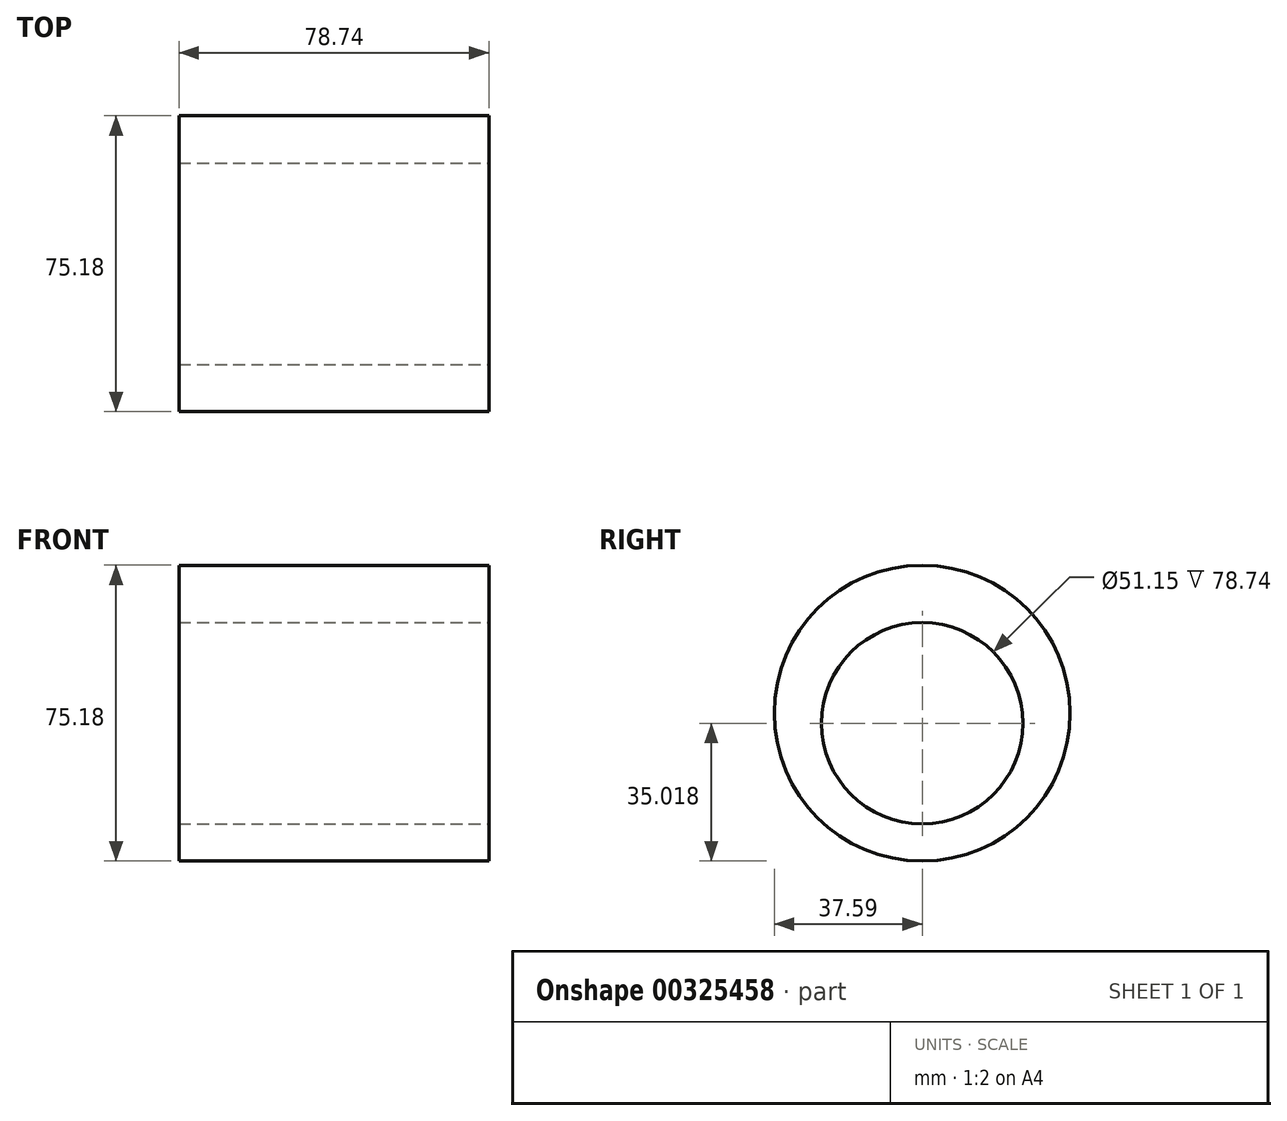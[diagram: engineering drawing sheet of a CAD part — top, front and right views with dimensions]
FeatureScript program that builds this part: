
annotation { "Feature Type Name" : "Feature", "Feature Type Description" : "" }
export const myFeature = defineFeature(function(context is Context, id is Id, definition is map)
    precondition{}
    {
        {
            var Q0;
            Q0=qCreatedBy(makeId("Right.planeOp"),FACE);
            var sketch = newSketch(context, id + "F0", { "sketchPlane" : qUnion([Q0])});
            skCircle(sketch, "E0", {"center": v(0, -2.57) * mm, "radius": 25.57 * mm});
            skCircle(sketch, "E1", {"center": v(0, 0) * mm, "radius": 37.59 * mm});
            skSolve(sketch);
        }
        {
            var Q0;
            Q0 = qSketchRegion(id + "F0", true);
            extrude(context, id + "F1", {"entities" : qUnion([Q0]), "oppositeDirection" : true, "depth" : 78.74 * mm});
        }
    });
